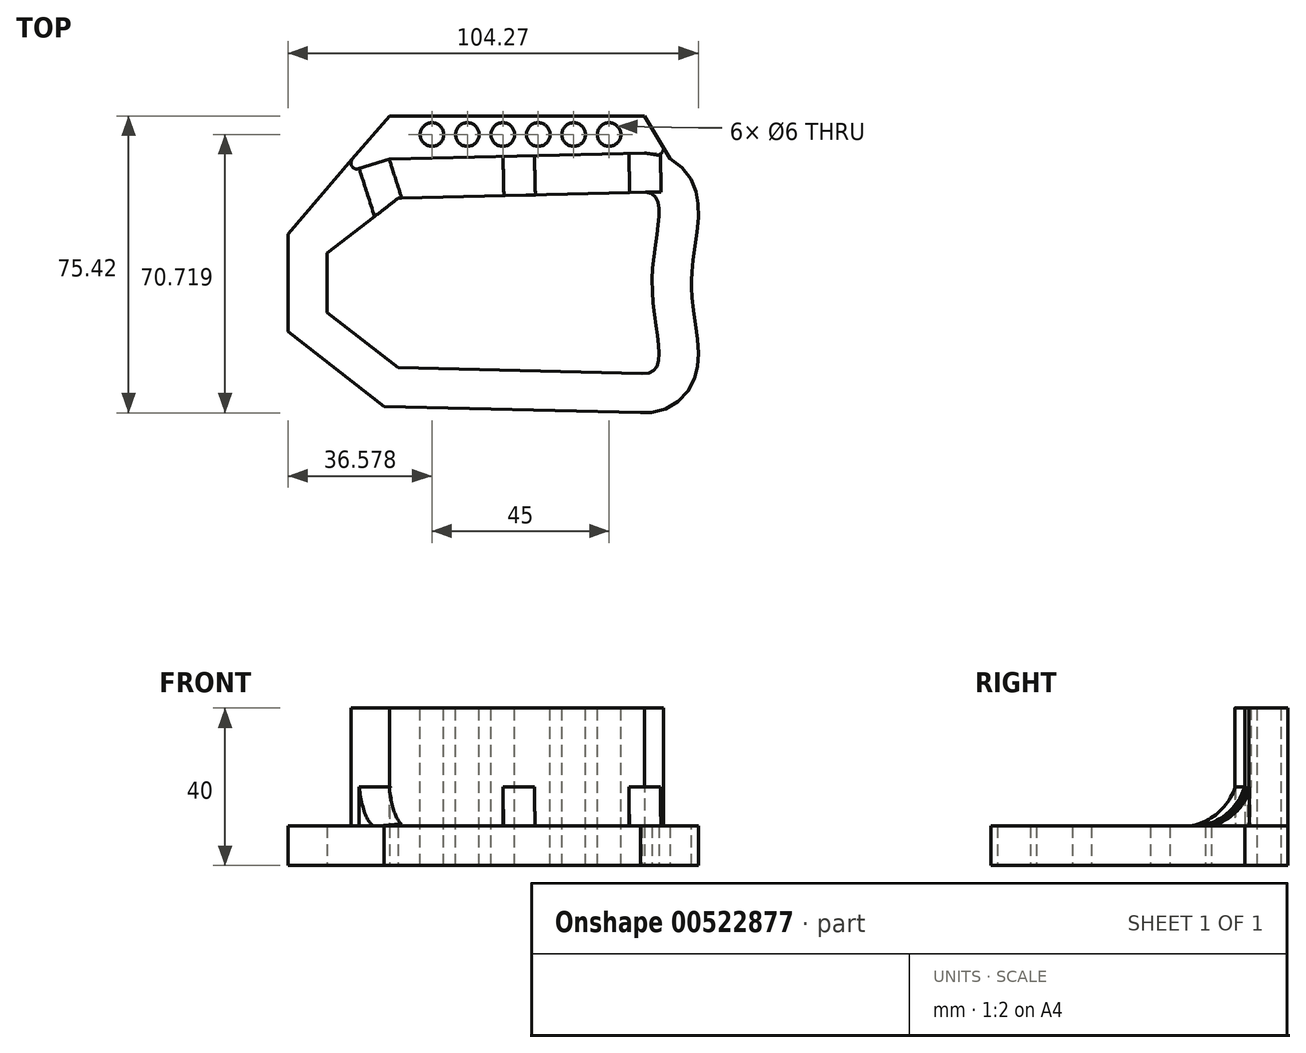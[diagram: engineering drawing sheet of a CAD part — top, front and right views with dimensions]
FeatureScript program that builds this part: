
annotation { "Feature Type Name" : "Feature", "Feature Type Description" : "" }
export const myFeature = defineFeature(function(context is Context, id is Id, definition is map)
    precondition{}
    {
        {
            var Q0;
            Q0=qCreatedBy(makeId("Top.planeOp"),FACE);
            var sketch = newSketch(context, id + "F0", { "sketchPlane" : qUnion([Q0])});
            skPoint(sketch, "E0.middle", {"position": v(0, 0) * mm});
            skLineSegment(sketch, "E1", {"start": v(-22, 21.5) * mm, "end": v(40, 23) * mm});
            skLineSegment(sketch, "E2", {"start": v(-22, -21.5) * mm, "end": v(40, -23) * mm});
            skLineSegment(sketch, "E3.bottom", {"start": v(-40, -7.5) * mm, "end": v(-40, -7.5) * mm});
            skLineSegment(sketch, "E3.top", {"start": v(-40, 7.5) * mm, "end": v(-40, 7.5) * mm});
            skLineSegment(sketch, "E3.left", {"start": v(-40, -7.5) * mm, "end": v(-40, 7.5) * mm});
            skLineSegment(sketch, "E3.right", {"start": v(-40, 7.5) * mm, "end": v(-40, -7.5) * mm});
            skPoint(sketch, "E3.middle", {"position": v(-40, 0) * mm});
            skLineSegment(sketch, "E4", {"start": v(-22, 21.5) * mm, "end": v(-40, 7.5) * mm});
            skLineSegment(sketch, "E5", {"start": v(-40, -7.5) * mm, "end": v(-22, -21.5) * mm});
            skFitSpline(sketch, "E6", {"points": [v(40, 23) * mm, v(42.5, 0) * mm, v(40, -23) * mm], "startDerivative": vector(46.5, 3.2) * mm, "endDerivative": vector(-46.5, 3.2) * mm});
            skPoint(sketch, "E0.right.end.orphan", {"position": v(40, 0) * mm});
            skLineSegment(sketch, "E7.1", {"start": v(-25.54, -31.42) * mm, "end": v(40.59, -33.02) * mm});
            skLineSegment(sketch, "E7.2", {"start": v(-50, -12.4) * mm, "end": v(-25.54, -31.42) * mm});
            skFitSpline(sketch, "E7.3", {"points": [v(39.31, 32.98) * mm, v(39.86, 33.01) * mm, v(40.99, 33.04) * mm, v(42.81, 32.89) * mm, v(44.75, 32.46) * mm, v(46.75, 31.69) * mm, v(48.68, 30.53) * mm, v(50.37, 29.06) * mm, v(51.7, 27.4) * mm, v(52.68, 25.7) * mm, v(53.34, 24.07) * mm, v(53.77, 22.55) * mm, v(54.03, 21.15) * mm, v(54.22, 19.42) * mm, v(54.26, 17.47) * mm, v(54.14, 15.3) * mm, v(53.93, 13.24) * mm, v(53.66, 11.23) * mm, v(53.38, 9.25) * mm, v(53.1, 7.29) * mm, v(52.86, 5.37) * mm, v(52.7, 3.8) * mm, v(52.6, 2.6) * mm, v(52.54, 1.7) * mm, v(52.51, 0.98) * mm, v(52.5, 0.41) * mm, v(52.5, 0) * mm, v(52.5, -0.41) * mm, v(52.51, -0.98) * mm, v(52.54, -1.7) * mm, v(52.6, -2.6) * mm, v(52.7, -3.8) * mm, v(52.86, -5.37) * mm, v(53.1, -7.29) * mm, v(53.38, -9.25) * mm, v(53.66, -11.23) * mm, v(53.93, -13.24) * mm, v(54.14, -15.3) * mm, v(54.26, -17.47) * mm, v(54.22, -19.42) * mm, v(54.03, -21.15) * mm, v(53.77, -22.55) * mm, v(53.34, -24.07) * mm, v(52.68, -25.7) * mm, v(51.7, -27.4) * mm, v(50.36, -29.06) * mm, v(48.68, -30.53) * mm, v(46.75, -31.69) * mm, v(44.75, -32.46) * mm, v(42.8, -32.89) * mm, v(40.99, -33.04) * mm, v(39.86, -33.01) * mm, v(39.31, -32.98) * mm]});
            skLineSegment(sketch, "E7.4", {"start": v(-50, 12.4) * mm, "end": v(-50, -12.4) * mm});
            skLineSegment(sketch, "E8.top", {"start": v(-24.21, 42.38) * mm, "end": v(40.59, 42.38) * mm});
            skPoint(sketch, "E9.top.end.orphan", {"position": v(22, 21.5) * mm});
            skPoint(sketch, "E9.bottom.end.orphan", {"position": v(22, -21.5) * mm});
            skLineSegment(sketch, "E10.trimOffspring", {"start": v(-40, 7.5) * mm, "end": v(-40, 0) * mm});
            skPoint(sketch, "E0.left.start.orphan", {"position": v(-40, 23) * mm});
            skPoint(sketch, "E11.trimOffspring.end.orphan", {"position": v(-40, -23) * mm});
            skLineSegment(sketch, "E12", {"start": v(40.59, 42.38) * mm, "end": v(47.14, 31.42) * mm});
            skLineSegment(sketch, "E13", {"start": v(-24.21, 42.38) * mm, "end": v(-50, 12.4) * mm});
            skPoint(sketch, "E14.start.orphan", {"position": v(-25.54, 31.42) * mm});
            skPoint(sketch, "E15.orphan", {"position": v(40.59, 33.02) * mm});
            skSolve(sketch);
        }
        {
            var Q0;
            Q0=qSketchRegion(id+"F0",true);
            extrude(context, id + "F1", {"entities" : qUnion([Q0]), "depth" : 10 * mm, "offsetDistance" : 25 * mm});
        }
        {
            var Q0;
            Q0=makeQuery(id+"F1.opExtrude","CAP_FACE",FACE,{"disambiguationData":[OSD([sQuery(id+"F0.wireOp",EDGE,"E1"),sQuery(id+"F0.wireOp",EDGE,"E2"),sQuery(id+"F0.wireOp",EDGE,"E3.right"),sQuery(id+"F0.wireOp",EDGE,"E4"),sQuery(id+"F0.wireOp",EDGE,"E5"),sQuery(id+"F0.wireOp",EDGE,"E6"),sQuery(id+"F0.wireOp",EDGE,"E7.1"),sQuery(id+"F0.wireOp",EDGE,"E7.2"),sQuery(id+"F0.wireOp",EDGE,"E7.3"),sQuery(id+"F0.wireOp",EDGE,"E7.4"),sQuery(id+"F0.wireOp",EDGE,"E8.top"),sQuery(id+"F0.wireOp",EDGE,"E10.trimOffspring"),sQuery(id+"F0.wireOp",EDGE,"E12"),sQuery(id+"F0.wireOp",EDGE,"E13")])],"isStart":false});
            var sketch = newSketch(context, id + "F2", { "sketchPlane" : qUnion([Q0])});
            skLineSegment(sketch, "E16.bottom", {"start": v(-24.21, 42.38) * mm, "end": v(40.57, 42.36) * mm});
            skLineSegment(sketch, "E16.top", {"start": v(-24.21, 31.5) * mm, "end": v(40.59, 33) * mm});
            skFitSpline(sketch, "E17", {"points": [v(40.59, 33) * mm, v(47.14, 31.42) * mm, v(50.41, 28.91) * mm, v(51.97, 26.89) * mm], "startDerivative": vector(17.08, -2.64) * mm, "endDerivative": vector(6.98, -10.23) * mm});
            skLineSegment(sketch, "E18", {"start": v(45.14, 34.75) * mm, "end": v(40.57, 42.36) * mm});
            skLineSegment(sketch, "E19", {"start": v(-24.21, 31.5) * mm, "end": v(-32.06, 29) * mm});
            skLineSegment(sketch, "E20", {"start": v(-33.65, 31.4) * mm, "end": v(-24.21, 42.38) * mm});
            skPoint(sketch, "E21.visualSharp", {"position": v(-37.1, 27.39) * mm});
            skArc(sketch, "E21.filletArc", {"start": v(-33.65, 31.4) * mm, "mid": v(-33.77, 29.6) * mm, "end": v(-32.06, 29) * mm});
            skArc(sketch, "E22.filletArc", {"start": v(43.57, 32.5) * mm, "mid": v(45.08, 33.11) * mm, "end": v(45.14, 34.75) * mm});
            skSolve(sketch);
        }
        {
            var Q0;
            Q0=makeQuery(id+"F2.imprint","IMPRINT",FACE,{"disambiguationData":[TD([[makeQuery(id+"F2.imprint","IMPRINT",EDGE,{"derivedFrom":sQuery(id+"F2.wireOp",EDGE,"E16.bottom")}),-1.0]])]});
            extrude(context, id + "F3", {"entities" : qUnion([Q0]), "operationType" : NewBodyOperationType.ADD, "depth" : 30 * mm, "offsetDistance" : 25 * mm});
        }
        {
            var Q0;
            Q0=makeQuery(id+"F3.opExtrude","CAP_FACE",FACE,{"disambiguationData":[OSD([sQuery(id+"F2.wireOp",EDGE,"E16.bottom"),sQuery(id+"F2.wireOp",EDGE,"E16.top"),sQuery(id+"F2.wireOp",EDGE,"E17"),sQuery(id+"F2.wireOp",EDGE,"E18"),sQuery(id+"F2.wireOp",EDGE,"E19"),sQuery(id+"F2.wireOp",EDGE,"E20")])],"isStart":false});
            var sketch = newSketch(context, id + "F4", { "sketchPlane" : qUnion([Q0])});
            skLineSegment(sketch, "E23", {"start": v(-22.42, 37.68) * mm, "end": v(40.58, 37.68) * mm});
            skPoint(sketch, "E24.orphan", {"position": v(-20.63, 43.86) * mm});
            skPoint(sketch, "E25.start.orphan", {"position": v(-24.21, 31.5) * mm});
            skPoint(sketch, "E26.orphan", {"position": v(40.59, 33) * mm});
            skPoint(sketch, "E27.start.orphan", {"position": v(40.57, 42.36) * mm});
            skCircle(sketch, "E28", {"center": v(-13.42, 37.68) * mm, "radius": 3 * mm});
            skCircle(sketch, "E29", {"center": v(-4.42, 37.68) * mm, "radius": 3 * mm});
            skCircle(sketch, "E30", {"center": v(4.58, 37.68) * mm, "radius": 3 * mm});
            skCircle(sketch, "E31", {"center": v(13.58, 37.68) * mm, "radius": 3 * mm});
            skCircle(sketch, "E32", {"center": v(22.58, 37.68) * mm, "radius": 3 * mm});
            skCircle(sketch, "E33", {"center": v(31.58, 37.68) * mm, "radius": 3 * mm});
            skSolve(sketch);
        }
        {
            var Q0;
            Q0=qSketchRegion(id+"F4",true);
            extrude(context, id + "F5", {"entities" : qUnion([Q0]), "operationType" : NewBodyOperationType.REMOVE, "oppositeDirection" : true, "depth" : 43 * mm, "offsetDistance" : 25 * mm});
        }
        {
            var Q0;
            Q0=makeQuery(id+"F3.opExtrude","SWEPT_FACE",FACE,{"disambiguationData":[OSD([sQuery(id+"F2.wireOp",EDGE,"E16.top")])]});
            var sketch = newSketch(context, id + "F6", { "sketchPlane" : qUnion([Q0])});
            skLineSegment(sketch, "E34.bottom", {"start": v(13.36, 20) * mm, "end": v(5.36, 20) * mm});
            skLineSegment(sketch, "E34.left", {"start": v(13.36, 20) * mm, "end": v(13.36, 10) * mm});
            skLineSegment(sketch, "E34.right", {"start": v(5.36, 20) * mm, "end": v(5.36, 10) * mm});
            skPoint(sketch, "E34.middle", {"position": v(8.93, 10) * mm});
            skLineSegment(sketch, "E35", {"start": v(5.36, 10) * mm, "end": v(13.36, 10) * mm});
            skSolve(sketch);
        }
        {
            var Q0;
            Q0=qSketchRegion(id+"F6",true);
            extrude(context, id + "F7", {"entities" : qUnion([Q0]), "operationType" : NewBodyOperationType.ADD, "depth" : 10 * mm, "offsetDistance" : 25 * mm});
        }
        {
            var Q0;
            Q0=makeQuery(id+"F7.opExtrude","SWEPT_FACE",FACE,{"disambiguationData":[OSD([sQuery(id+"F6.wireOp",EDGE,"E34.right")])]});
            var sketch = newSketch(context, id + "F8", { "sketchPlane" : qUnion([Q0])});
            skArc(sketch, "E36", {"start": v(-32.05, 20) * mm, "mid": v(-28.3, 13.75) * mm, "end": v(-22.05, 10) * mm});
            skLineSegment(sketch, "E37", {"start": v(-32.05, 20) * mm, "end": v(-22.05, 20) * mm});
            skLineSegment(sketch, "E38", {"start": v(-22.05, 20) * mm, "end": v(-22.05, 10) * mm});
            skSolve(sketch);
        }
        {
            var Q0;
            Q0=qSketchRegion(id+"F8",true);
            extrude(context, id + "F9", {"entities" : qUnion([Q0]), "operationType" : NewBodyOperationType.REMOVE, "oppositeDirection" : true, "depth" : 25 * mm, "offsetDistance" : 25 * mm});
        }
        {
            var Q0;
            Q0=makeQuery(id+"F3.opExtrude","SWEPT_FACE",FACE,{"disambiguationData":[OSD([sQuery(id+"F2.wireOp",EDGE,"E19")])]});
            var sketch = newSketch(context, id + "F10", { "sketchPlane" : qUnion([Q0])});
            skLineSegment(sketch, "E39.bottom", {"start": v(-21.56, 20) * mm, "end": v(-13.56, 20) * mm});
            skLineSegment(sketch, "E39.left", {"start": v(-21.56, 20) * mm, "end": v(-21.56, 10) * mm});
            skLineSegment(sketch, "E39.right", {"start": v(-13.56, 20) * mm, "end": v(-13.56, 10) * mm});
            skPoint(sketch, "E39.middle", {"position": v(-17.61, 10) * mm});
            skLineSegment(sketch, "E40", {"start": v(-21.56, 10) * mm, "end": v(-13.56, 10) * mm});
            skSolve(sketch);
        }
        {
            var Q0;
            Q0=qSketchRegion(id+"F10",true);
            extrude(context, id + "F11", {"entities" : qUnion([Q0]), "operationType" : NewBodyOperationType.ADD, "depth" : 12.8 * mm, "offsetDistance" : 25 * mm});
        }
        {
            var Q0;
            Q0=makeQuery(id+"F11.opExtrude","SWEPT_FACE",FACE,{"disambiguationData":[OSD([sQuery(id+"F10.wireOp",EDGE,"E39.left")])]});
            var sketch = newSketch(context, id + "F12", { "sketchPlane" : qUnion([Q0])});
            skArc(sketch, "E41", {"start": v(-37.37, 20) * mm, "mid": v(-32.44, 13.12) * mm, "end": v(-24.57, 10) * mm});
            skSolve(sketch);
        }
        {
            var Q0;
            Q0=qSketchRegion(id+"F12",true);
            var Q1;
            Q1=makeQuery(id+"F12.imprint","IMPRINT",FACE,{"disambiguationData":[TD([[makeQuery(id+"F12.imprint","IMPRINT",EDGE,{"derivedFrom":sQuery(id+"F12.wireOp",EDGE,"E41")}),1.0]])]});
            extrude(context, id + "F13", {"entities" : qUnion([Q0, Q1]), "operationType" : NewBodyOperationType.REMOVE, "oppositeDirection" : true, "depth" : 8.3 * mm, "offsetDistance" : 25 * mm});
        }
        {
            var Q0;
            Q0=makeQuery(id+"F3.opExtrude","SWEPT_FACE",FACE,{"disambiguationData":[OSD([sQuery(id+"F2.wireOp",EDGE,"E16.top")])]});
            var sketch = newSketch(context, id + "F14", { "sketchPlane" : qUnion([Q0])});
            skLineSegment(sketch, "E42.bottom", {"start": v(37.34, 20) * mm, "end": v(45.34, 20) * mm});
            skLineSegment(sketch, "E42.left", {"start": v(37.34, 20) * mm, "end": v(37.34, 10) * mm});
            skLineSegment(sketch, "E42.right", {"start": v(45.34, 20) * mm, "end": v(45.34, 10) * mm});
            skPoint(sketch, "E42.middle", {"position": v(41.34, 10) * mm});
            skLineSegment(sketch, "E43", {"start": v(37.34, 10) * mm, "end": v(45.34, 10) * mm});
            skSolve(sketch);
        }
        {
            var Q0;
            Q0=qSketchRegion(id+"F14",true);
            extrude(context, id + "F15", {"entities" : qUnion([Q0]), "operationType" : NewBodyOperationType.ADD, "depth" : 10 * mm, "offsetDistance" : 25 * mm});
        }
        {
            var Q0;
            Q0=makeQuery(id+"F15.opExtrude","SWEPT_FACE",FACE,{"disambiguationData":[OSD([sQuery(id+"F14.wireOp",EDGE,"E42.right")])]});
            var sketch = newSketch(context, id + "F16", { "sketchPlane" : qUnion([Q0])});
            skArc(sketch, "E44", {"start": v(22.05, 10) * mm, "mid": v(28.3, 13.75) * mm, "end": v(32.05, 20) * mm});
            skLineSegment(sketch, "E45", {"start": v(32.05, 20) * mm, "end": v(22.05, 20) * mm});
            skLineSegment(sketch, "E46", {"start": v(22.05, 20) * mm, "end": v(22.05, 10) * mm});
            skSolve(sketch);
        }
        {
            var Q0;
            Q0=qSketchRegion(id+"F16",true);
            extrude(context, id + "F17", {"entities" : qUnion([Q0]), "operationType" : NewBodyOperationType.REMOVE, "oppositeDirection" : true, "depth" : 9.2 * mm, "offsetDistance" : 25 * mm});
        }
        {
            var Q0;
            Q0=makeQuery(id+"F11.opExtrude","SWEPT_FACE",FACE,{"disambiguationData":[OSD([sQuery(id+"F10.wireOp",EDGE,"E40")])]});
            var sketch = newSketch(context, id + "F18", { "sketchPlane" : qUnion([Q0])});
            skLineSegment(sketch, "E47", {"start": v(-27.95, -16.87) * mm, "end": v(-22, -21.5) * mm});
            skLineSegment(sketch, "E48", {"start": v(-22, -21.5) * mm, "end": v(-21.1, -21.52) * mm});
            skLineSegment(sketch, "E49", {"start": v(-21.1, -21.52) * mm, "end": v(-20.39, -19.28) * mm});
            skLineSegment(sketch, "E50", {"start": v(-20.39, -19.28) * mm, "end": v(-27.95, -16.87) * mm});
            skSolve(sketch);
        }
        {
            var Q0;
            Q0 = qSketchRegion(id + "F18", true);
            extrude(context, id + "F19", {"entities" : qUnion([Q0]), "operationType" : NewBodyOperationType.REMOVE, "oppositeDirection" : true, "depth" : 25 * mm, "offsetDistance" : 25 * mm});
        }
    });
